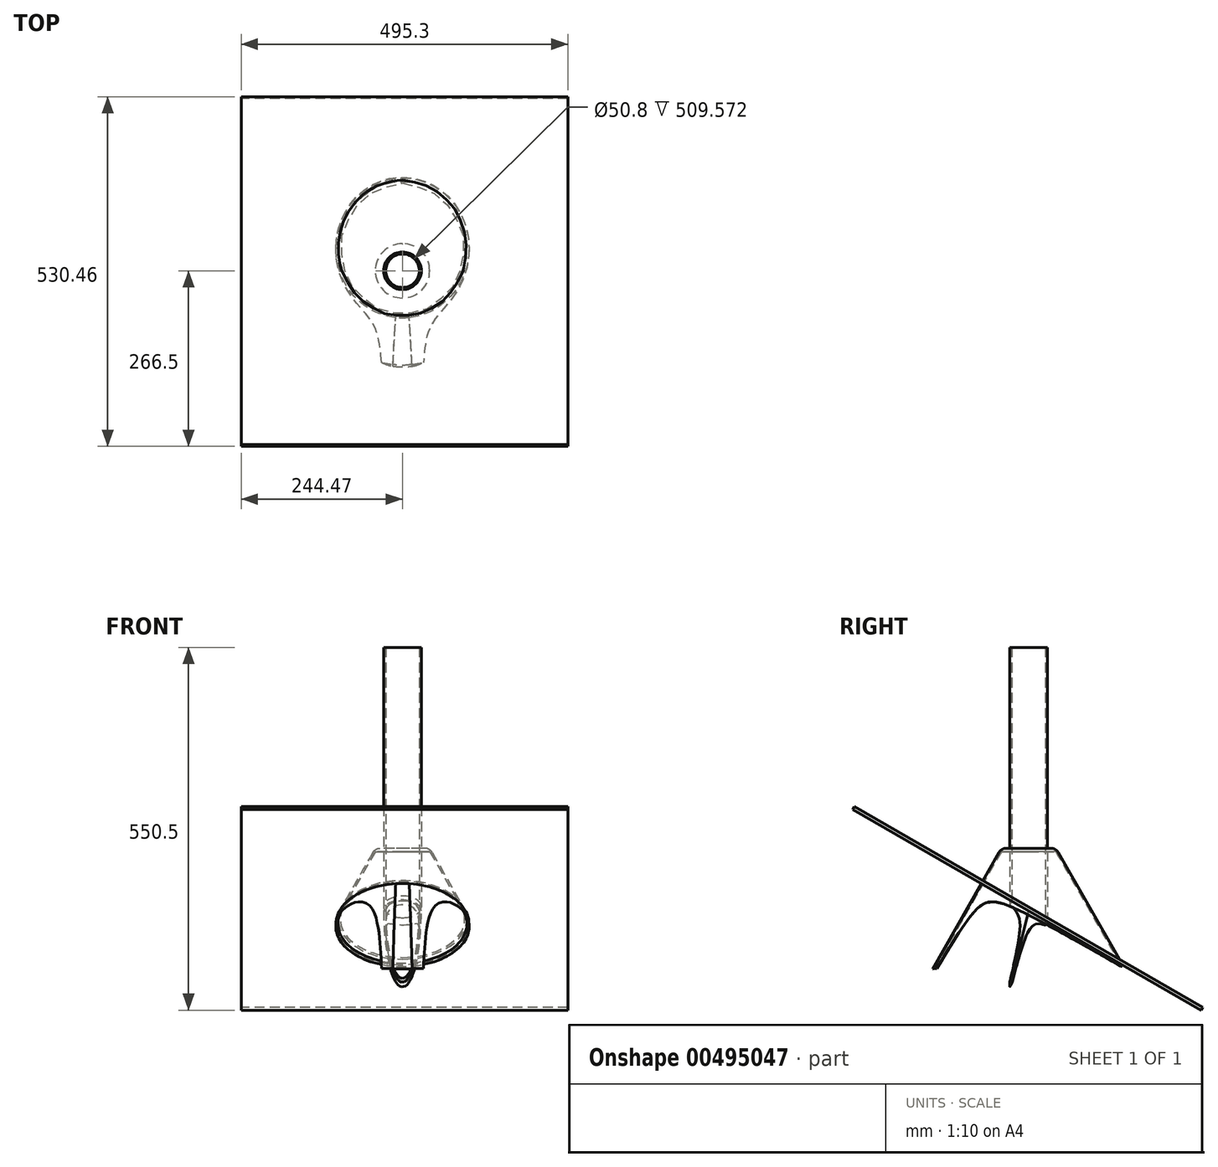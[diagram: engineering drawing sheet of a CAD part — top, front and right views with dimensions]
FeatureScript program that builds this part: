
annotation { "Feature Type Name" : "Feature", "Feature Type Description" : "" }
export const myFeature = defineFeature(function(context is Context, id is Id, definition is map)
    precondition{}
    {
        {
            var Q0;
            Q0=qCreatedBy(makeId("Top.planeOp"),FACE);
            var sketch = newSketch(context, id + "F0", { "sketchPlane" : qUnion([Q0])});
            skCircle(sketch, "E0", {"center": v(0, 0) * mm, "radius": 25.4 * mm});
            skCircle(sketch, "E1", {"center": v(0, 0) * mm, "radius": 28.58 * mm});
            skCircle(sketch, "E2", {"center": v(0, 0) * mm, "radius": 31.75 * mm});
            skSolve(sketch);
        }
        {
            var Q0;
            Q0=makeQuery(id+"F0.imprint","IMPRINT",FACE,{"disambiguationData":[TD([[makeQuery(id+"F0.imprint","IMPRINT",EDGE,{"derivedFrom":sQuery(id+"F0.wireOp",EDGE,"E0")}),-1.0]])]});
            extrude(context, id + "F1", {"entities" : qUnion([Q0]), "endBound" : BoundingType.SYMMETRIC, "depth" : 609.6 * mm, "offsetDistance" : 25.4 * mm});
        }
        {
            var Q0;
            Q0=qCreatedBy(makeId("Front.planeOp"),FACE);
            var sketch = newSketch(context, id + "F2", { "sketchPlane" : qUnion([Q0])});
            skLineSegment(sketch, "E3", {"start": v(0, 0) * mm, "end": v(-28.58, 0) * mm});
            skLineSegment(sketch, "E4", {"start": v(-28.58, 0) * mm, "end": v(-41.28, 0) * mm});
            skLineSegment(sketch, "E5", {"start": v(-41.27, 0) * mm, "end": v(-41.27, -88.9) * mm});
            skLineSegment(sketch, "E6", {"start": v(-41.27, -88.9) * mm, "end": v(-92.07, -88.9) * mm});
            skLineSegment(sketch, "E7", {"start": v(-92.07, -88.9) * mm, "end": v(-41.27, 0) * mm});
            skLineSegment(sketch, "E8", {"start": v(-92.07, -88.9) * mm, "end": v(-244.47, -88.9) * mm});
            skLineSegment(sketch, "E9", {"start": v(-28.58, 0) * mm, "end": v(-28.58, -5.08) * mm});
            skLineSegment(sketch, "E10", {"start": v(-28.58, -5.08) * mm, "end": v(-41.28, -5.08) * mm});
            skLineSegment(sketch, "E11", {"start": v(-41.28, -5.08) * mm, "end": v(-92.08, -93.98) * mm});
            skLineSegment(sketch, "E12", {"start": v(-92.07, -93.98) * mm, "end": v(-244.47, -93.98) * mm});
            skLineSegment(sketch, "E13", {"start": v(-244.47, -88.9) * mm, "end": v(-244.47, -93.98) * mm});
            skLineSegment(sketch, "E14", {"start": v(0, 0) * mm, "end": v(0, -155.45) * mm});
            skLineSegment(sketch, "E15", {"start": v(-92.07, -88.9) * mm, "end": v(-92.07, -93.98) * mm});
            skLineSegment(sketch, "E16", {"start": v(-92.08, -93.98) * mm, "end": v(-142.75, -182.66) * mm});
            skLineSegment(sketch, "E17", {"start": v(-92.07, -88.9) * mm, "end": v(-145.72, -182.77) * mm});
            skLineSegment(sketch, "E18", {"start": v(-145.72, -182.77) * mm, "end": v(-142.75, -182.66) * mm});
            skSolve(sketch);
        }
        {
            var Q0;
            {var subQ0=sQuery(id+"F2.wireOp",EDGE,"E7");Q0=makeQuery(id+"F2.imprint","IMPRINT",FACE,{"disambiguationData":[TD([[makeQuery(id+"F2.imprint","IMPRINT",EDGE,{"derivedFrom":subQ0}),-1.0]])]});}
            var Q1;
            {var subQ0=sQuery(id+"F2.wireOp",EDGE,"E16");Q1=makeQuery(id+"F2.imprint","IMPRINT",FACE,{"disambiguationData":[TD([[makeQuery(id+"F2.imprint","IMPRINT",EDGE,{"derivedFrom":subQ0}),-1.0]])]});}
            var Q2;
            {var subQ0=sQuery(id+"F2.wireOp",EDGE,"E15");Q2=makeQuery(id+"F2.imprint","IMPRINT",FACE,{"disambiguationData":[TD([[makeQuery(id+"F2.imprint","IMPRINT",EDGE,{"derivedFrom":subQ0}),1.0]])]});}
            var Q3;
            {var subQ0=sQuery(id+"F2.wireOp",EDGE,"E15");Q3=makeQuery(id+"F2.imprint","IMPRINT",FACE,{"disambiguationData":[TD([[makeQuery(id+"F2.imprint","IMPRINT",EDGE,{"derivedFrom":subQ0}),-1.0]])]});}
            var Q4;
            {var subQ0=sQuery(id+"F2.wireOp",EDGE,"E4");Q4=makeQuery(id+"F2.imprint","IMPRINT",FACE,{"disambiguationData":[TD([[makeQuery(id+"F2.imprint","IMPRINT",EDGE,{"derivedFrom":subQ0}),1.0]])]});}
            var Q5;
            Q5=sQuery(id+"F2.wireOp",EDGE,"E14");
            revolve(context, id + "F3", {"entities" : qUnion([Q0, Q1, Q2, Q3, Q4]), "axis" : qUnion([Q5]), "revolveType" : RevolveType.FULL});
        }
        {
            var Q0;
            Q0=makeQuery(id+"F2.imprint","IMPRINT",FACE,{"disambiguationData":[TD([[makeQuery(id+"F2.imprint","IMPRINT",EDGE,{"derivedFrom":sQuery(id+"F2.wireOp",EDGE,"E8")}),1.0]])]});
            var Q1;
            {var subQ0=sQuery(id+"F2.wireOp",EDGE,"E15");Q1=makeQuery(id+"F2.imprint","IMPRINT",FACE,{"disambiguationData":[TD([[makeQuery(id+"F2.imprint","IMPRINT",EDGE,{"derivedFrom":subQ0}),-1.0]])]});}
            extrude(context, id + "F4", {"entities" : qUnion([Q0, Q1]), "endBound" : BoundingType.SYMMETRIC, "depth" : 609.6 * mm, "offsetDistance" : 25.4 * mm});
        }
        {
            var Q0;
            Q0=makeQuery(id+"F4.opExtrude","SWEPT_BODY",BODY,{"disambiguationData":[OSD([sQuery(id+"F2.wireOp",EDGE,"E8"),sQuery(id+"F2.wireOp",EDGE,"E12"),sQuery(id+"F2.wireOp",EDGE,"E13"),sQuery(id+"F2.wireOp",EDGE,"E15")])]});
            var Q1;
            Q1=sQuery(id+"F2.wireOp",EDGE,"E8");
            transform(context, id + "F5", {"entities" : qUnion([Q0]), "transformType" : TransformType.ROTATION, "transformAxis" : qUnion([Q1]), "angle" : 30 * degree, "makeCopy" : false});
        }
        {
            var Q0;
            Q0=makeQuery(id+"F4.opExtrude","SWEPT_FACE",FACE,{"disambiguationData":[OSD([sQuery(id+"F2.wireOp",EDGE,"E15")])]});
            extrude(context, id + "F6", {"entities" : qUnion([Q0]), "operationType" : NewBodyOperationType.ADD, "depth" : 342.9 * mm, "offsetDistance" : 25.4 * mm});
        }
        {
            var Q0;
            {var subQ0=sQuery(id+"F2.wireOp",EDGE,"E12");Q0=makeQuery(id+"F6.boolean.opBoolean","MERGE",FACE,{"derivedFrom":[makeQuery(id+"F4.opExtrude","SWEPT_FACE",FACE,{"disambiguationData":[OSD([subQ0])]}),makeQuery(id+"F6.opExtrude","SWEPT_FACE",FACE,{"disambiguationData":[OSD([sQuery(id+"F2.wireOp",EDGE,"E11"),subQ0,sQuery(id+"F2.wireOp",EDGE,"E15"),sQuery(id+"F2.wireOp",EDGE,"E16")])]})]});}
            extrude(context, id + "F7", {"entities" : qUnion([Q0]), "operationType" : NewBodyOperationType.REMOVE, "depth" : 609.6 * mm, "offsetDistance" : 25.4 * mm});
        }
        {
            var Q0;
            Q0=makeQuery(id+"F0.imprint","IMPRINT",FACE,{"disambiguationData":[TD([[makeQuery(id+"F0.imprint","IMPRINT",EDGE,{"derivedFrom":sQuery(id+"F0.wireOp",EDGE,"E0")}),1.0]])]});
            extrude(context, id + "F8", {"entities" : qUnion([Q0]), "operationType" : NewBodyOperationType.REMOVE, "endBound" : BoundingType.SYMMETRIC, "oppositeDirection" : true, "depth" : 609.6 * mm, "offsetDistance" : 25.4 * mm});
        }
        {
            var Q0;
            Q0=makeQuery(id+"F3.opRevolve","SWEPT_EDGE",EDGE,{"disambiguationData":[OSD([sQuery(id+"F2.wireOp",EDGE,"E4"),sQuery(id+"F2.wireOp",EDGE,"E5"),sQuery(id+"F2.wireOp",EDGE,"E7")])]});
            fillet(context, id + "F9", {"entities" : qUnion([Q0]), "radius" : 12.7 * mm, "tangentPropagation" : true, "allowEdgeOverflow" : false});
        }
    });
